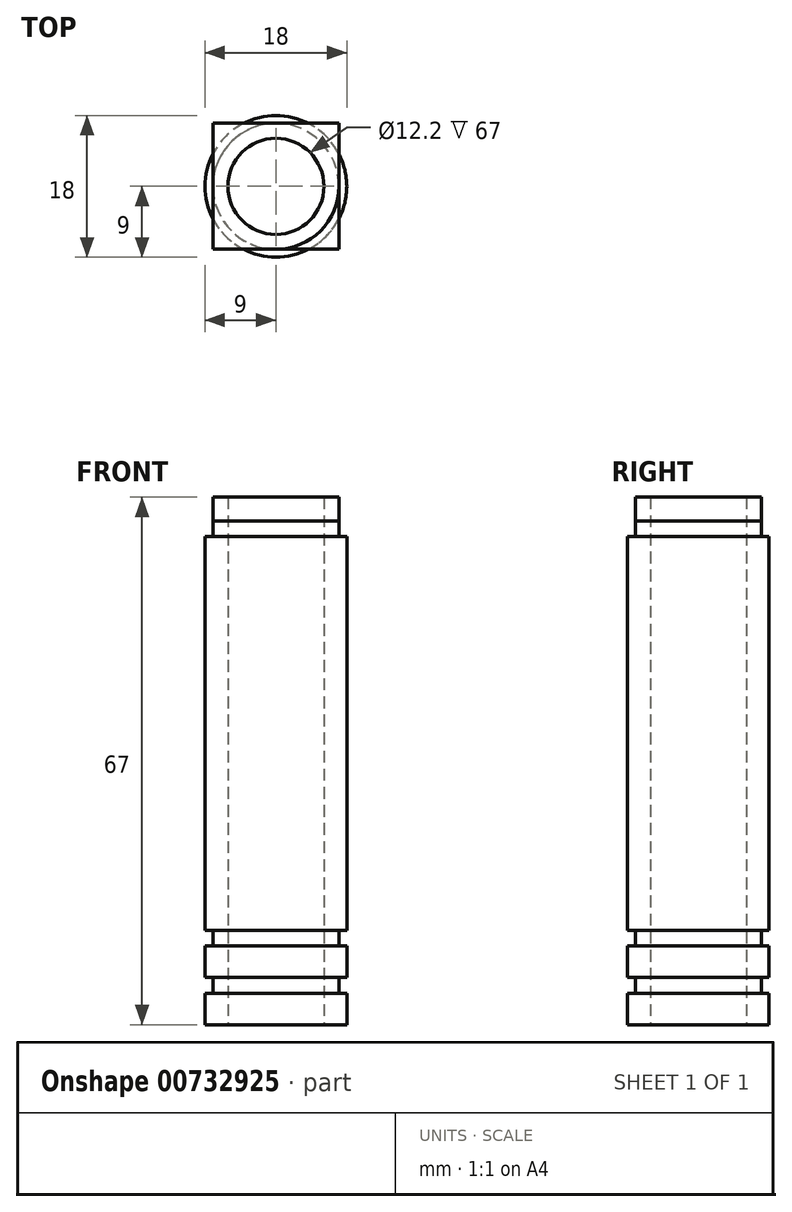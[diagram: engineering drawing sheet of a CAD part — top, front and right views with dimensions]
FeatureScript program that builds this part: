
annotation { "Feature Type Name" : "Feature", "Feature Type Description" : "" }
export const myFeature = defineFeature(function(context is Context, id is Id, definition is map)
    precondition{}
    {
        {
            var Q0;
            Q0=qCreatedBy(makeId("Top.planeOp"),FACE);
            var sketch = newSketch(context, id + "F0", { "sketchPlane" : qUnion([Q0])});
            skCircle(sketch, "E0", {"center": v(0, 0) * mm, "radius": 6.1 * mm});
            skCircle(sketch, "E1", {"center": v(0, 0) * mm, "radius": 9 * mm});
            skSolve(sketch);
        }
        {
            var Q0;
            Q0=makeQuery(id+"F0.imprint","IMPRINT",FACE,{"disambiguationData":[TD([[makeQuery(id+"F0.imprint","IMPRINT",EDGE,{"derivedFrom":sQuery(id+"F0.wireOp",EDGE,"E0")}),-1.0]])]});
            extrude(context, id + "F1", {"entities" : qUnion([Q0]), "depth" : 4 * mm, "offsetDistance" : 25 * mm});
        }
        {
            var Q0;
            Q0=makeQuery(id+"F1.opExtrude","CAP_FACE",FACE,{"disambiguationData":[OSD([sQuery(id+"F0.wireOp",EDGE,"E0"),sQuery(id+"F0.wireOp",EDGE,"E1")])],"isStart":false});
            var sketch = newSketch(context, id + "F2", { "sketchPlane" : qUnion([Q0])});
            skCircle(sketch, "E2", {"center": v(0, 0) * mm, "radius": 8 * mm});
            skSolve(sketch);
        }
        {
            var Q0;
            Q0=makeQuery(id+"F2.imprint","IMPRINT",FACE,{"disambiguationData":[TD([[makeQuery(id+"F2.imprint","IMPRINT",EDGE,{"derivedFrom":sQuery(id+"F2.wireOp",EDGE,"E2")}),1.0]])]});
            extrude(context, id + "F3", {"entities" : qUnion([Q0]), "operationType" : NewBodyOperationType.ADD, "depth" : 2 * mm, "offsetDistance" : 25 * mm});
        }
        {
            var Q0;
            Q0=makeQuery(id+"F3.opExtrude","CAP_FACE",FACE,{"disambiguationData":[OSD([sQuery(id+"F0.wireOp",EDGE,"E0"),sQuery(id+"F2.wireOp",EDGE,"E2")])],"isStart":false});
            var sketch = newSketch(context, id + "F4", { "sketchPlane" : qUnion([Q0])});
            skCircle(sketch, "E3", {"center": v(0, 0) * mm, "radius": 9 * mm});
            skSolve(sketch);
        }
        {
            var Q0;
            Q0=makeQuery(id+"F4.imprint","IMPRINT",FACE,{"disambiguationData":[TD([[makeQuery(id+"F4.imprint","IMPRINT",EDGE,{"derivedFrom":makeQuery(id+"F3.opExtrude","CAP_EDGE",EDGE,{"disambiguationData":[OSD([sQuery(id+"F2.wireOp",EDGE,"E2")])],"isStart":false})}),1.0]])]});
            var Q1;
            Q1=makeQuery(id+"F4.imprint","IMPRINT",FACE,{"disambiguationData":[TD([[makeQuery(id+"F4.imprint","IMPRINT",EDGE,{"derivedFrom":sQuery(id+"F4.wireOp",EDGE,"E3")}),1.0]])]});
            extrude(context, id + "F5", {"entities" : qUnion([Q0, Q1]), "operationType" : NewBodyOperationType.ADD, "depth" : 4 * mm, "offsetDistance" : 25 * mm});
        }
        {
            var Q0;
            Q0=makeQuery(id+"F5.opExtrude","CAP_FACE",FACE,{"disambiguationData":[OSD([sQuery(id+"F0.wireOp",EDGE,"E0"),sQuery(id+"F4.wireOp",EDGE,"E3")])],"isStart":false});
            var sketch = newSketch(context, id + "F6", { "sketchPlane" : qUnion([Q0])});
            skCircle(sketch, "E4", {"center": v(0, 0) * mm, "radius": 8 * mm});
            skSolve(sketch);
        }
        {
            var Q0;
            Q0=makeQuery(id+"F6.imprint","IMPRINT",FACE,{"disambiguationData":[TD([[makeQuery(id+"F6.imprint","IMPRINT",EDGE,{"derivedFrom":sQuery(id+"F6.wireOp",EDGE,"E4")}),1.0]])]});
            extrude(context, id + "F7", {"entities" : qUnion([Q0]), "operationType" : NewBodyOperationType.ADD, "depth" : 2 * mm, "offsetDistance" : 25 * mm});
        }
        {
            var Q0;
            Q0=makeQuery(id+"F7.opExtrude","CAP_FACE",FACE,{"disambiguationData":[OSD([sQuery(id+"F0.wireOp",EDGE,"E0"),sQuery(id+"F6.wireOp",EDGE,"E4")])],"isStart":false});
            var sketch = newSketch(context, id + "F8", { "sketchPlane" : qUnion([Q0])});
            skCircle(sketch, "E5", {"center": v(0, 0) * mm, "radius": 9 * mm});
            skSolve(sketch);
        }
        {
            var Q0;
            Q0=makeQuery(id+"F8.imprint","IMPRINT",FACE,{"disambiguationData":[TD([[makeQuery(id+"F8.imprint","IMPRINT",EDGE,{"derivedFrom":makeQuery(id+"F7.opExtrude","CAP_EDGE",EDGE,{"disambiguationData":[OSD([sQuery(id+"F6.wireOp",EDGE,"E4")])],"isStart":false})}),1.0]])]});
            var Q1;
            Q1=makeQuery(id+"F8.imprint","IMPRINT",FACE,{"disambiguationData":[TD([[makeQuery(id+"F8.imprint","IMPRINT",EDGE,{"derivedFrom":sQuery(id+"F8.wireOp",EDGE,"E5")}),1.0]])]});
            extrude(context, id + "F9", {"entities" : qUnion([Q0, Q1]), "operationType" : NewBodyOperationType.ADD, "depth" : 50 * mm, "offsetDistance" : 25 * mm});
        }
        {
            var Q0;
            Q0=makeQuery(id+"F9.opExtrude","CAP_FACE",FACE,{"disambiguationData":[OSD([sQuery(id+"F0.wireOp",EDGE,"E0"),sQuery(id+"F8.wireOp",EDGE,"E5")])],"isStart":false});
            var sketch = newSketch(context, id + "F10", { "sketchPlane" : qUnion([Q0])});
            skCircle(sketch, "E6", {"center": v(0, 0) * mm, "radius": 8 * mm});
            skSolve(sketch);
        }
        {
            var Q0;
            Q0=makeQuery(id+"F10.imprint","IMPRINT",FACE,{"disambiguationData":[TD([[makeQuery(id+"F10.imprint","IMPRINT",EDGE,{"derivedFrom":sQuery(id+"F10.wireOp",EDGE,"E6")}),1.0]])]});
            extrude(context, id + "F11", {"entities" : qUnion([Q0]), "operationType" : NewBodyOperationType.ADD, "depth" : 2 * mm, "offsetDistance" : 25 * mm});
        }
        {
            var Q0;
            Q0=makeQuery(id+"F11.opExtrude","CAP_FACE",FACE,{"disambiguationData":[OSD([sQuery(id+"F0.wireOp",EDGE,"E0"),sQuery(id+"F10.wireOp",EDGE,"E6")])],"isStart":false});
            var sketch = newSketch(context, id + "F12", { "sketchPlane" : qUnion([Q0])});
            skLineSegment(sketch, "E7.bottom", {"start": v(-8, 8) * mm, "end": v(8, 8) * mm});
            skLineSegment(sketch, "E7.top", {"start": v(-8, -8) * mm, "end": v(8, -8) * mm});
            skLineSegment(sketch, "E7.left", {"start": v(-8, 8) * mm, "end": v(-8, -8) * mm});
            skLineSegment(sketch, "E7.right", {"start": v(8, 8) * mm, "end": v(8, -8) * mm});
            skPoint(sketch, "E7.middle", {"position": v(0, 0) * mm});
            skSolve(sketch);
        }
        {
            var Q0;
            Q0=makeQuery(id+"F12.imprint","IMPRINT",FACE,{"disambiguationData":[TD([[makeQuery(id+"F12.imprint","IMPRINT",EDGE,{"derivedFrom":makeQuery(id+"F11.opExtrude","CAP_EDGE",EDGE,{"disambiguationData":[OSD([sQuery(id+"F0.wireOp",EDGE,"E0")])],"isStart":false})}),-1.0]])]});
            var Q1;
            {var subQ0=sQuery(id+"F12.wireOp",EDGE,"E7.left");var subQ1=sQuery(id+"F12.wireOp",EDGE,"E7.bottom");var subQ2=makeQuery(id+"F12.imprint","INTERSECT",VERTEX,{"derivedFrom":[subQ1,subQ0]});Q1=makeQuery(id+"F12.imprint","IMPRINT",FACE,{"disambiguationData":[TD([[makeQuery(id+"F12.imprint","IMPRINT",EDGE,{"disambiguationData":[TD([[subQ2,-1.0]])],"derivedFrom":subQ1}),-1.0]])]});}
            var Q2;
            {var subQ0=sQuery(id+"F12.wireOp",EDGE,"E7.left");var subQ1=sQuery(id+"F12.wireOp",EDGE,"E7.top");var subQ2=makeQuery(id+"F12.imprint","INTERSECT",VERTEX,{"derivedFrom":[subQ1,subQ0]});Q2=makeQuery(id+"F12.imprint","IMPRINT",FACE,{"disambiguationData":[TD([[makeQuery(id+"F12.imprint","IMPRINT",EDGE,{"disambiguationData":[TD([[subQ2,-1.0]])],"derivedFrom":subQ1}),1.0]])]});}
            var Q3;
            {var subQ0=sQuery(id+"F12.wireOp",EDGE,"E7.right");var subQ1=sQuery(id+"F12.wireOp",EDGE,"E7.top");var subQ2=makeQuery(id+"F12.imprint","INTERSECT",VERTEX,{"derivedFrom":[subQ1,subQ0]});Q3=makeQuery(id+"F12.imprint","IMPRINT",FACE,{"disambiguationData":[TD([[makeQuery(id+"F12.imprint","IMPRINT",EDGE,{"disambiguationData":[TD([[subQ2,1.0]])],"derivedFrom":subQ1}),1.0]])]});}
            var Q4;
            {var subQ0=sQuery(id+"F12.wireOp",EDGE,"E7.right");var subQ1=sQuery(id+"F12.wireOp",EDGE,"E7.bottom");var subQ2=makeQuery(id+"F12.imprint","INTERSECT",VERTEX,{"derivedFrom":[subQ1,subQ0]});Q4=makeQuery(id+"F12.imprint","IMPRINT",FACE,{"disambiguationData":[TD([[makeQuery(id+"F12.imprint","IMPRINT",EDGE,{"disambiguationData":[TD([[subQ2,1.0]])],"derivedFrom":subQ1}),-1.0]])]});}
            extrude(context, id + "F13", {"entities" : qUnion([Q0, Q1, Q2, Q3, Q4]), "operationType" : NewBodyOperationType.ADD, "depth" : 3 * mm, "offsetDistance" : 25 * mm});
        }
    });
